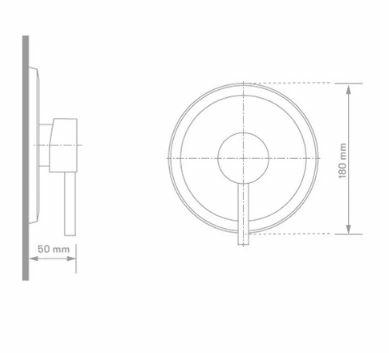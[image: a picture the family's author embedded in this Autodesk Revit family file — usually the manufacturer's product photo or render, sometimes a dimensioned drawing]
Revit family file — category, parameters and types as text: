
# Revit family: 01-3401-11SR DUCHA MONOMANDO SST SIN REGADERA VICCTOR
name_source: partatom
category: Aparatos sanitarios
revit_build: Autodesk Revit 2018 (Build: 20170223_1515(x64)
units: mm (PartAtom-declared; Revit-internal decimal feet)

## family parameters
Anfitrión = Cara
Compartido = No
Corte con vacíos al cargar = No
Cota de conector redondo = Diámetro de uso
Número OmniClass = 23.31.11.00
Punto de cálculo de habitación = No
Tipo de pieza = Normal

## types (1)
- 01-3401-11SR
    Alto = 112.5 mm  [stored 0.369094 ft]
    Ancho = 145.1 mm
    Conexión AC = Sí
    Conexión AF = Sí
    Conexión de residuos = No
    Conexión de ventilación = No
    Descripción = Griferia Monomando Ducha
    Elevación por defecto = 0 mm  [stored 0 ft]
    Fabricante = Gricol
    Imagen de tipo = <Ninguno>
    Link Ficha Tecnica = http://infotecnica.gricol.com
    Metal Zamak Cromado = Metal Zamak Cromado
    Modelo = 01-3401-11SR
    Plastico ABS Cromado = Plastico ABS Cromado
    Product Name = DUCHA MONOMANDO SST SIN REGADERA VICCTOR
    Profundidad = 50 mm
    URL = https://www.gricol.com

note: [stored X ft] marks values corroborated as IEEE doubles in the binary element streams (Revit-internal decimal feet)

## geometry (parser evidence)
native form markers: Blend x2, Sweep x5
no freeform markers — native parametric forms only
